# Revit family: Shower-Handshower_Kit-KOHLER-PURIST-K-14590T_1
name_source: partatom
category: Plumbing Fixtures
revit_build: Autodesk Revit 2017 (Build: 20160225_1515(x64)
units: mm (PartAtom-declared; Revit-internal decimal feet)

## family parameters
Cut with Voids When Loaded = No
Host = Face
OmniClass Number = 23.31.17.00
OmniClass Title = Showers
Part Type = Normal
Room Calculation Point = No
Round Connector Dimension = Use Diameter
Shared = No

## types (3) — shared parameters
ADA Compliant = No
Assembly Code = D2010700
CW Connection = Yes
Cold Water Inlet = Cold Water Inlet
Date Modified = 08/25/2021
Default Elevation = 42"
Description = PURIST EXPOSED SHOWER FAUCET
Drain Included = No
Flow Rate = 2 GPM
HW Connection = Yes
Handle Clearance = 3"
Height = 17 3/16"
Hot Water Inlet = Hot Water Inlet
Length = 9 9/16"
Manufacturer = KOHLER Co.
Master Format 2014 = 22 42 23
Master Format 2014 Name = Residential Showers
Material = Premium Metal Construction
Pressure = 125.00 psi
Product Name = PURIST
URL = http://www.kohler.com.cn
Vent Connection = No
Waste Connection = No
Waste Water Outlet = Waste Water Outlet
WaterSense Certified = No
Width = 5 7/8"

## per-type parameters (varying)
| type | Finish | Model | Type |
| CP-Polished Chrome | Kohler-Metal-CP-Polished_Chrome | K-14590T-4-CP | 1 |
| BGD-Romankin | Kohler-Metal-BGD-Romankin | K-14590T-4-BGD | 2 |
| PGD-Eternal Gold | Kohler-Metal-PGD-Eternal_Gold | K-14590T-4-PGD | 3 |

## geometry (parser evidence)
native form markers: Sweep x5
no freeform markers — native parametric forms only
